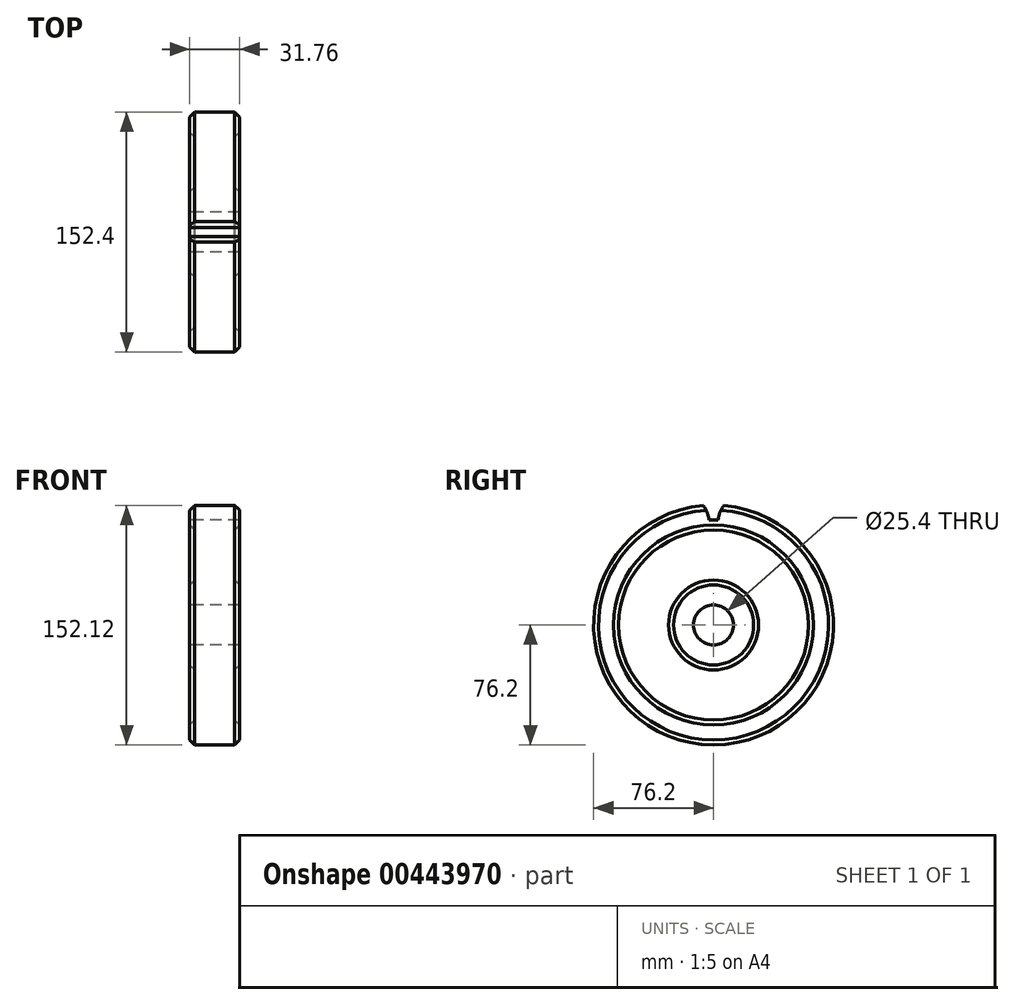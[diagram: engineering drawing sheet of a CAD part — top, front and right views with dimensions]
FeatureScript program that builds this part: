
annotation { "Feature Type Name" : "Feature", "Feature Type Description" : "" }
export const myFeature = defineFeature(function(context is Context, id is Id, definition is map)
    precondition{}
    {
        {
            var Q0;
            Q0=qCreatedBy(makeId("Top.planeOp"),FACE);
            var sketch = newSketch(context, id + "F0", { "sketchPlane" : qUnion([Q0])});
            skLineSegment(sketch, "E0", {"start": v(0, 0) * mm, "end": v(0, 63.5) * mm});
            skLineSegment(sketch, "E1", {"start": v(0, 63.5) * mm, "end": v(12.7, 63.5) * mm});
            skLineSegment(sketch, "E2", {"start": v(12.7, 63.5) * mm, "end": v(15.88, 60.32) * mm});
            skLineSegment(sketch, "E3", {"start": v(15.88, 60.32) * mm, "end": v(15.88, 50.8) * mm});
            skLineSegment(sketch, "E4", {"start": v(15.88, 50.8) * mm, "end": v(12.7, 47.62) * mm});
            skLineSegment(sketch, "E5", {"start": v(12.7, 47.62) * mm, "end": v(12.7, 15.88) * mm});
            skLineSegment(sketch, "E6", {"start": v(12.7, 15.88) * mm, "end": v(15.88, 12.7) * mm});
            skLineSegment(sketch, "E7", {"start": v(15.88, 12.7) * mm, "end": v(15.88, 0) * mm});
            skLineSegment(sketch, "E8", {"start": v(15.88, 0) * mm, "end": v(0, 0) * mm});
            skLineSegment(sketch, "E9", {"start": v(0, 0) * mm, "end": v(0, -12.7) * mm});
            skLineSegment(sketch, "E10", {"start": v(0, -12.7) * mm, "end": v(15.88, -12.7) * mm});
            skLineSegment(sketch, "E11.MirrorCS", {"start": v(-12.7, 63.5) * mm, "end": v(-15.88, 60.32) * mm});
            skLineSegment(sketch, "E12.MirrorCS", {"start": v(-12.7, 15.88) * mm, "end": v(-15.88, 12.7) * mm});
            skLineSegment(sketch, "E13.MirrorCS", {"start": v(-12.7, 47.62) * mm, "end": v(-12.7, 15.88) * mm});
            skLineSegment(sketch, "E14.MirrorCS", {"start": v(-15.88, 12.7) * mm, "end": v(-15.87, 0) * mm});
            skLineSegment(sketch, "E15.MirrorCS", {"start": v(-15.88, 50.8) * mm, "end": v(-12.7, 47.62) * mm});
            skLineSegment(sketch, "E16.MirrorCS", {"start": v(-15.88, 60.32) * mm, "end": v(-15.88, 50.8) * mm});
            skLineSegment(sketch, "E17.MirrorCS", {"start": v(-15.88, 0) * mm, "end": v(0, 0) * mm});
            skLineSegment(sketch, "E18.MirrorCS", {"start": v(0, 63.5) * mm, "end": v(-12.7, 63.5) * mm});
            skSolve(sketch);
        }
        {
            var Q0;
            Q0=makeQuery(id+"F0.imprint","IMPRINT",FACE,{"disambiguationData":[TD([[makeQuery(id+"F0.imprint","IMPRINT",EDGE,{"derivedFrom":sQuery(id+"F0.wireOp",EDGE,"E0")}),-1.0]])]});
            var Q1;
            Q1=makeQuery(id+"F0.imprint","IMPRINT",FACE,{"disambiguationData":[TD([[makeQuery(id+"F0.imprint","IMPRINT",EDGE,{"derivedFrom":sQuery(id+"F0.wireOp",EDGE,"E0")}),1.0]])]});
            var Q2;
            Q2=sQuery(id+"F0.wireOp",EDGE,"E10");
            revolve(context, id + "F1", {"entities" : qUnion([Q0, Q1]), "axis" : qUnion([Q2]), "revolveType" : RevolveType.FULL});
        }
        {
            var Q0;
            Q0=makeQuery(id+"F1.opRevolve","SWEPT_FACE",FACE,{"disambiguationData":[OSD([sQuery(id+"F0.wireOp",EDGE,"E16.MirrorCS")])]});
            var sketch = newSketch(context, id + "F2", { "sketchPlane" : qUnion([Q0])});
            skLineSegment(sketch, "E19", {"start": v(12.7, 0) * mm, "end": v(12.7, 89.5) * mm});
            skLineSegment(sketch, "E20", {"start": v(12.7, 66.68) * mm, "end": v(15.56, 66.68) * mm});
            skArc(sketch, "E21", {"start": v(19.24, 75.92) * mm, "mid": v(16.78, 71.54) * mm, "end": v(15.56, 66.68) * mm});
            skLineSegment(sketch, "E22.MirrorCS", {"start": v(12.7, 133.35) * mm, "end": v(12.7, 43.84) * mm});
            skLineSegment(sketch, "E23.MirrorCS", {"start": v(12.7, 66.68) * mm, "end": v(9.84, 66.68) * mm});
            skArc(sketch, "E24.MirrorCS", {"start": v(6.16, 75.92) * mm, "mid": v(8.62, 71.54) * mm, "end": v(9.84, 66.68) * mm});
            skArc(sketch, "E25.0", {"start": v(19.24, 75.92) * mm, "mid": v(12.7, 76.2) * mm, "end": v(6.16, 75.92) * mm});
            skSolve(sketch);
        }
        {
            var Q0;
            {var subQ0=sQuery(id+"F2.wireOp",EDGE,"E25.0");var subQ5=sQuery(id+"F2.wireOp",EDGE,"E24.MirrorCS");var subQ7=makeQuery(id+"F2.imprint","INTERSECT",VERTEX,{"derivedFrom":[subQ5,subQ0]});Q0=makeQuery(id+"F2.imprint","IMPRINT",FACE,{"disambiguationData":[TD([[makeQuery(id+"F2.imprint","IMPRINT",EDGE,{"disambiguationData":[TD([[subQ7,1.0]])],"derivedFrom":subQ0}),1.0]])]});}
            var Q1;
            {var subQ0=sQuery(id+"F2.wireOp",EDGE,"E23.MirrorCS");Q1=makeQuery(id+"F2.imprint","IMPRINT",FACE,{"disambiguationData":[TD([[makeQuery(id+"F2.imprint","IMPRINT",EDGE,{"derivedFrom":subQ0}),-1.0]])]});}
            var Q2;
            {var subQ0=sQuery(id+"F2.wireOp",EDGE,"E20");Q2=makeQuery(id+"F2.imprint","IMPRINT",FACE,{"disambiguationData":[TD([[makeQuery(id+"F2.imprint","IMPRINT",EDGE,{"derivedFrom":subQ0}),1.0]])]});}
            var Q3;
            {var subQ0=sQuery(id+"F2.wireOp",EDGE,"E25.0");var subQ1=sQuery(id+"F2.wireOp",EDGE,"E21");var subQ2=makeQuery(id+"F2.imprint","INTERSECT",VERTEX,{"derivedFrom":[subQ1,subQ0]});Q3=makeQuery(id+"F2.imprint","IMPRINT",FACE,{"disambiguationData":[TD([[makeQuery(id+"F2.imprint","IMPRINT",EDGE,{"disambiguationData":[TD([[subQ2,-1.0]])],"derivedFrom":subQ0}),1.0]])]});}
            extrude(context, id + "F3", {"entities" : qUnion([Q0, Q1, Q2, Q3]), "operationType" : NewBodyOperationType.REMOVE, "endBound" : BoundingType.THROUGH_ALL, "oppositeDirection" : true, "depth" : 25.4 * mm});
        }
    });
